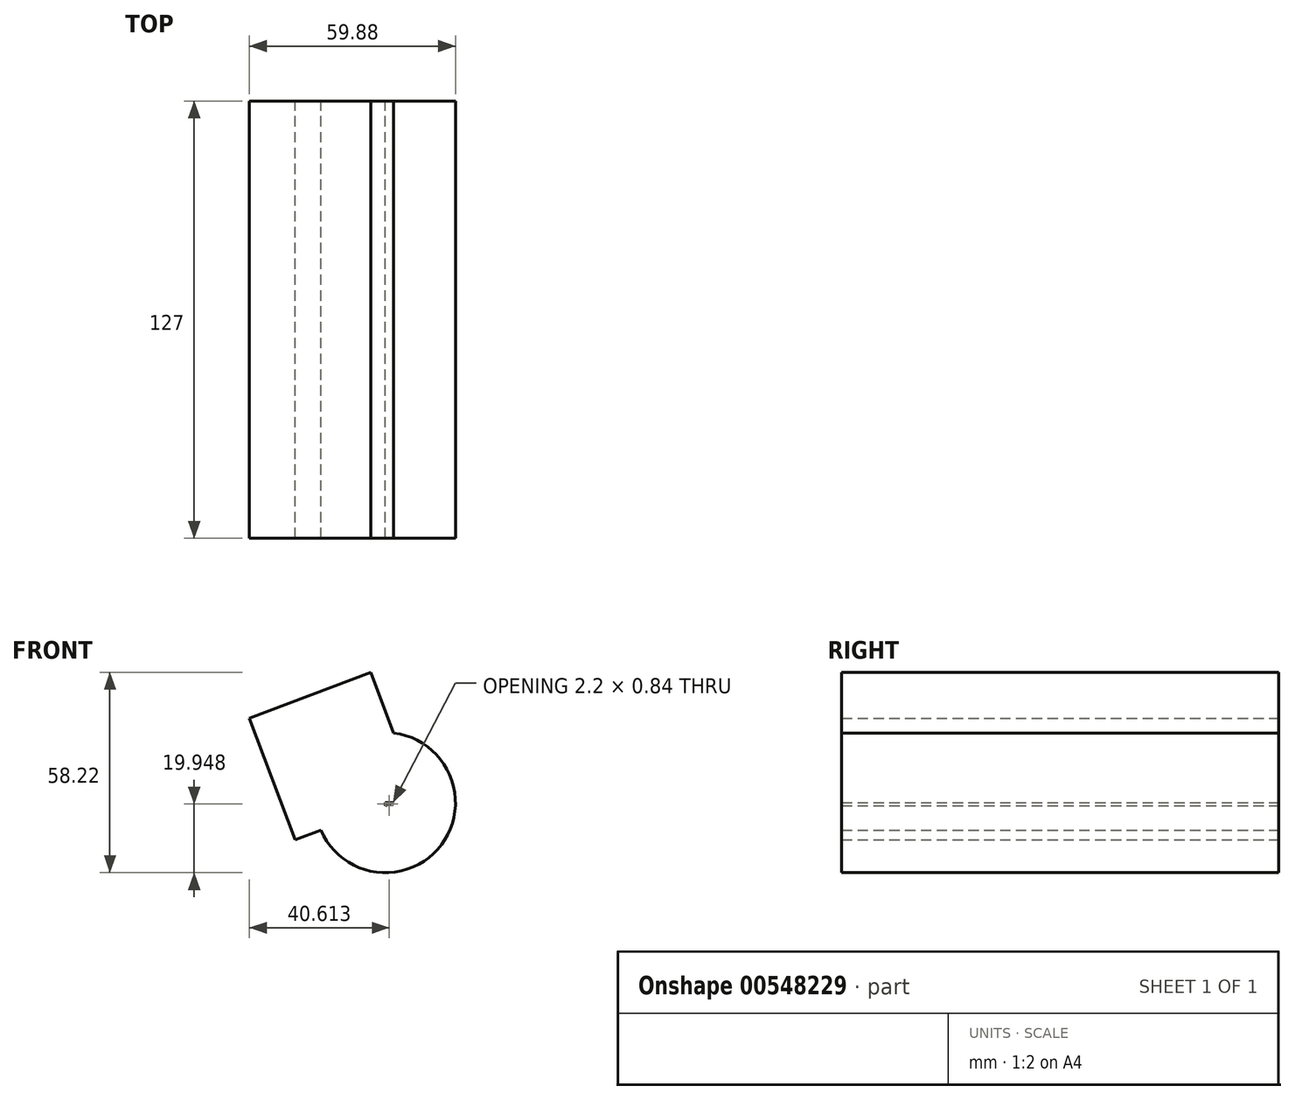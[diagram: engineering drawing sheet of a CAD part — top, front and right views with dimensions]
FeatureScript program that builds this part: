
annotation { "Feature Type Name" : "Feature", "Feature Type Description" : "" }
export const myFeature = defineFeature(function(context is Context, id is Id, definition is map)
    precondition{}
    {
        {
            var Q0;
            Q0=qCreatedBy(makeId("Front.planeOp"),FACE);
            var sketch = newSketch(context, id + "F0", { "sketchPlane" : qUnion([Q0])});
            skCircle(sketch, "E0", {"center": v(-15.02, 13.76) * mm, "radius": 20.37 * mm});
            skLineSegment(sketch, "E1.bottom", {"start": v(-15.02, 13.76) * mm, "end": v(0, 13.76) * mm});
            skLineSegment(sketch, "E1.top", {"start": v(-15.02, 0) * mm, "end": v(0, 0) * mm});
            skLineSegment(sketch, "E1.left", {"start": v(-15.02, 13.76) * mm, "end": v(-15.02, 0) * mm});
            skLineSegment(sketch, "E1.right", {"start": v(0, 13.76) * mm, "end": v(0, 0) * mm});
            skCircle(sketch, "E2.cCircle", {"center": v(-30.23, 27.3) * mm, "radius": 18.84 * mm, "construction": true});
            skLineSegment(sketch, "E2.0", {"start": v(-54.53, 38.23) * mm, "end": v(-19.3, 51.6) * mm});
            skLineSegment(sketch, "E2.1", {"start": v(-19.3, 51.6) * mm, "end": v(-5.93, 16.37) * mm});
            skLineSegment(sketch, "E2.2", {"start": v(-5.93, 16.37) * mm, "end": v(-41.16, 3) * mm});
            skLineSegment(sketch, "E2.3", {"start": v(-41.16, 3) * mm, "end": v(-54.53, 38.23) * mm});
            skPoint(sketch, "E2.0.midPoint", {"position": v(-36.92, 44.92) * mm});
            skSolve(sketch);
        }
        {
            var Q0;
            Q0 = qSketchRegion(id + "F0", true);
            extrude(context, id + "F1", {"entities" : qUnion([Q0]), "depth" : 127 * mm, "offsetDistance" : 25.4 * mm});
        }
    });
